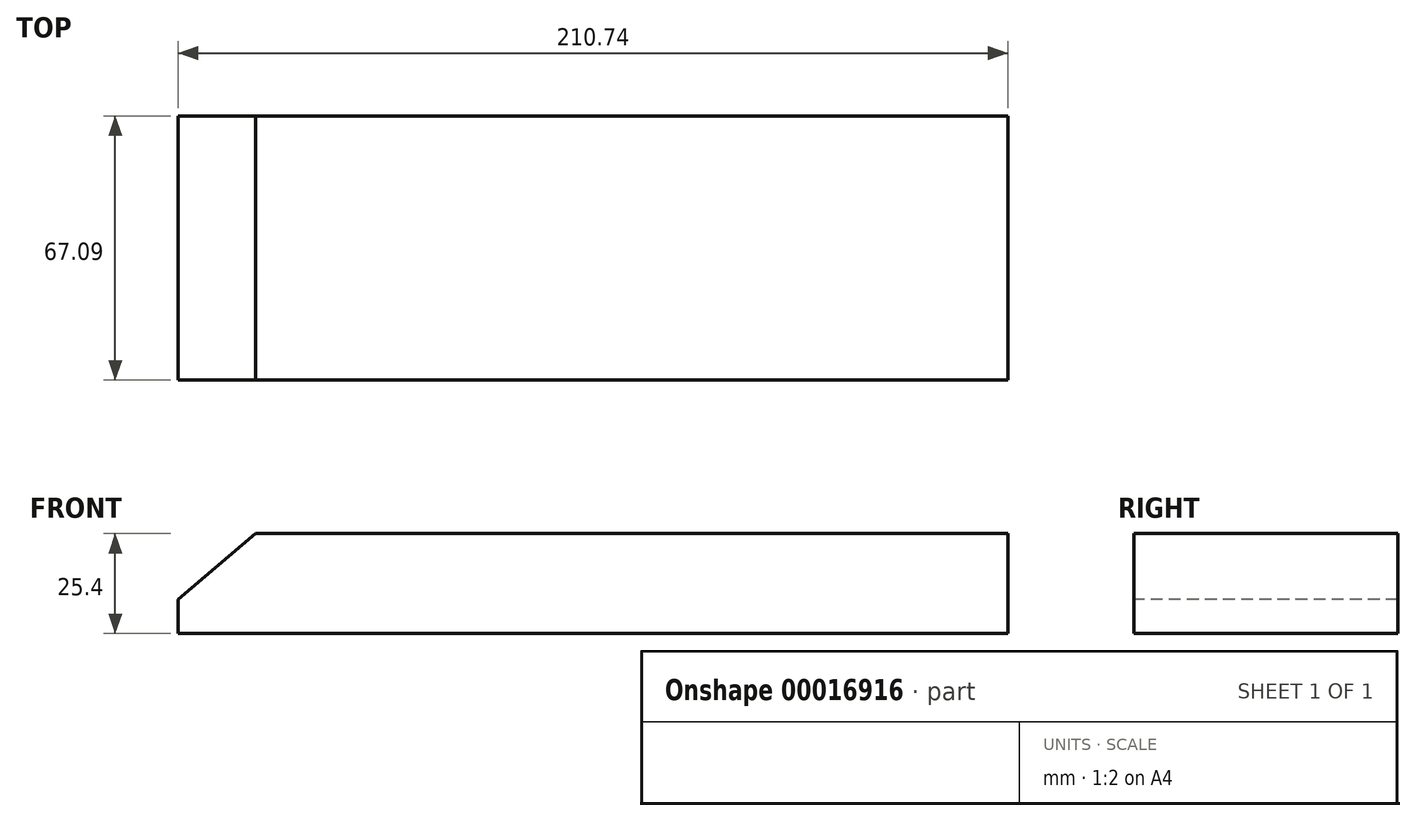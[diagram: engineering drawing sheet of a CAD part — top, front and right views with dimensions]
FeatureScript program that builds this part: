
annotation { "Feature Type Name" : "Feature", "Feature Type Description" : "" }
export const myFeature = defineFeature(function(context is Context, id is Id, definition is map)
    precondition{}
    {
        {
            var Q0;
            Q0=qCreatedBy(makeId("Top.planeOp"),FACE);
            var sketch = newSketch(context, id + "F0", { "sketchPlane" : qUnion([Q0])});
            skLineSegment(sketch, "E0.bottom", {"start": v(-112.62, 12.73) * mm, "end": v(98.12, 12.73) * mm});
            skLineSegment(sketch, "E0.top", {"start": v(-112.62, -54.36) * mm, "end": v(98.12, -54.36) * mm});
            skLineSegment(sketch, "E0.left", {"start": v(-112.62, 12.73) * mm, "end": v(-112.62, -54.36) * mm});
            skLineSegment(sketch, "E0.right", {"start": v(98.12, 12.73) * mm, "end": v(98.12, -54.36) * mm});
            skSolve(sketch);
        }
        {
            var Q0;
            Q0=makeQuery(id+"F0.imprint","IMPRINT",FACE,{"disambiguationData":[TD([[makeQuery(id+"F0.imprint","IMPRINT",EDGE,{"derivedFrom":sQuery(id+"F0.wireOp",EDGE,"E0.bottom")}),-1.0]])]});
            extrude(context, id + "F1", {"entities" : qUnion([Q0]), "depth" : 25.4 * mm});
        }
        {
            var Q0;
            Q0=makeQuery(id+"F1.opExtrude","SWEPT_FACE",FACE,{"disambiguationData":[OSD([sQuery(id+"F0.wireOp",EDGE,"E0.top")])]});
            var sketch = newSketch(context, id + "F2", { "sketchPlane" : qUnion([Q0])});
            skLineSegment(sketch, "E1", {"start": v(-112.62, 8.7) * mm, "end": v(-93.04, 25.4) * mm});
            skLineSegment(sketch, "E2", {"start": v(-122.1, 27.05) * mm, "end": v(-112.62, 8.7) * mm});
            skLineSegment(sketch, "E3", {"start": v(-122.1, 27.05) * mm, "end": v(-93.04, 25.4) * mm});
            skSolve(sketch);
        }
        {
            var Q0;
            {var subQ6=sQuery(id+"F2.wireOp",EDGE,"E2");Q0=makeQuery(id+"F2.imprint","IMPRINT",FACE,{"disambiguationData":[TD([[makeQuery(id+"F2.imprint","IMPRINT",EDGE,{"derivedFrom":subQ6}),1.0]])]});}
            var Q1;
            {var subQ2=sQuery(id+"F2.wireOp",EDGE,"E1");Q1=makeQuery(id+"F2.imprint","IMPRINT",FACE,{"disambiguationData":[TD([[makeQuery(id+"F2.imprint","IMPRINT",EDGE,{"derivedFrom":subQ2}),1.0]])]});}
            extrude(context, id + "F3", {"entities" : qUnion([Q0, Q1]), "operationType" : NewBodyOperationType.REMOVE, "endBound" : BoundingType.THROUGH_ALL, "oppositeDirection" : true, "depth" : 25.4 * mm});
        }
    });
